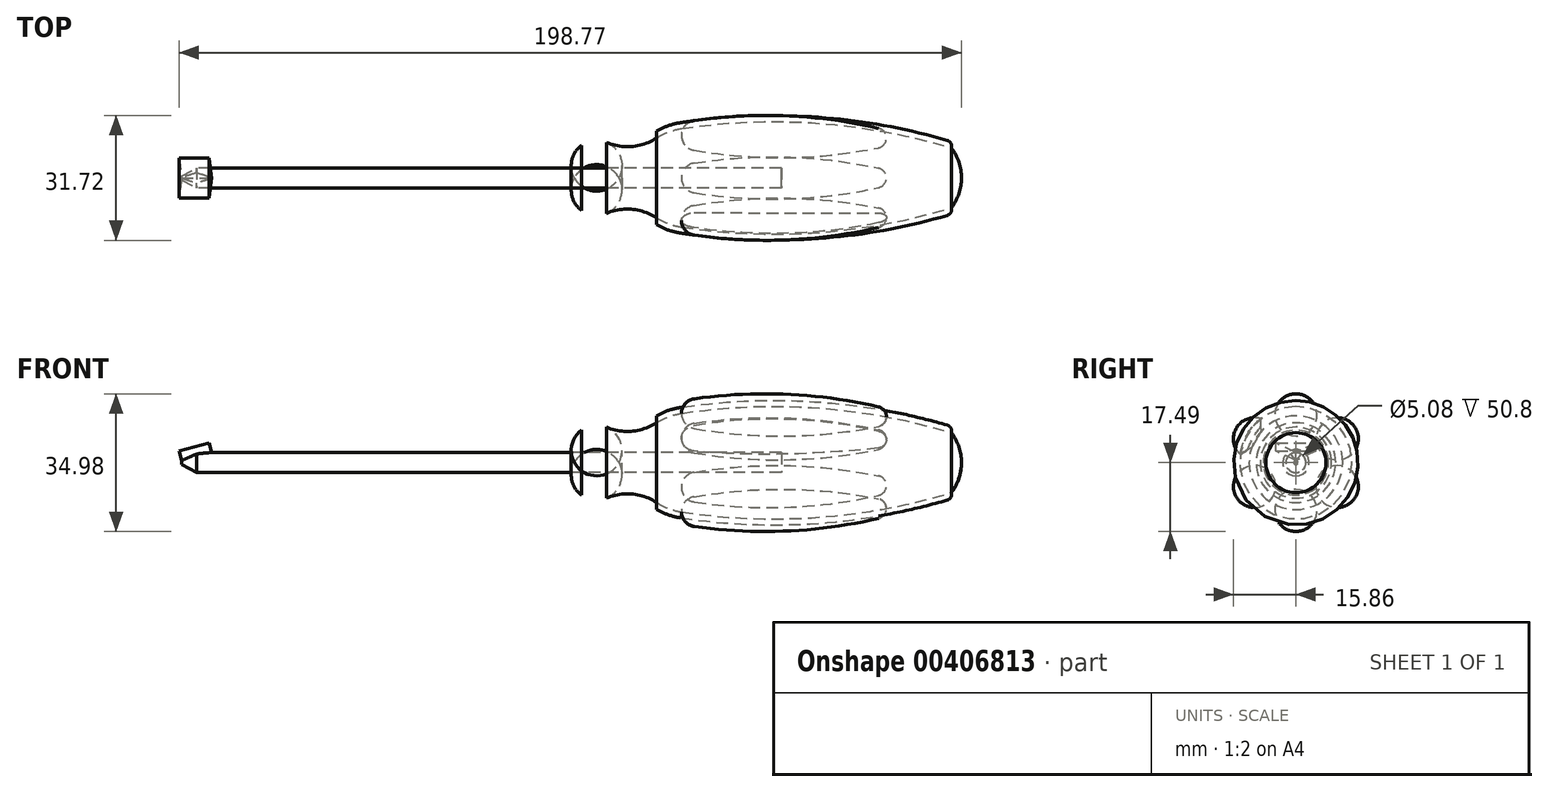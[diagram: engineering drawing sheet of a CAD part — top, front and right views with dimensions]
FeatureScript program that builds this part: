
annotation { "Feature Type Name" : "Feature", "Feature Type Description" : "" }
export const myFeature = defineFeature(function(context is Context, id is Id, definition is map)
    precondition{}
    {
        {
            var Q0;
            Q0=qCreatedBy(makeId("Front.planeOp"),FACE);
            var sketch = newSketch(context, id + "F0", { "sketchPlane" : qUnion([Q0])});
            skLineSegment(sketch, "E0", {"start": v(-101.6, 0) * mm, "end": v(96.52, 0) * mm});
            skLineSegment(sketch, "E1", {"start": v(96.52, 0) * mm, "end": v(117.55, 0) * mm, "construction": true});
            skLineSegment(sketch, "E2", {"start": v(50.8, 2.54) * mm, "end": v(-97.8, 2.54) * mm});
            skLineSegment(sketch, "E3", {"start": v(-101.6, 0.5) * mm, "end": v(-101.6, 0) * mm});
            skLineSegment(sketch, "E4", {"start": v(0, 2.54) * mm, "end": v(0, 8.25) * mm});
            skArc(sketch, "E5", {"start": v(6.35, 9.02) * mm, "mid": v(3.07, 9.48) * mm, "end": v(0, 8.25) * mm});
            skArc(sketch, "E6", {"start": v(6.35, 9.02) * mm, "mid": v(12.84, 7.99) * mm, "end": v(19.05, 10.11) * mm});
            skArc(sketch, "E7", {"start": v(25.4, 12.52) * mm, "mid": v(22.1, 11.65) * mm, "end": v(19.05, 10.11) * mm});
            skArc(sketch, "E8", {"start": v(93.98, 7.62) * mm, "mid": v(59.96, 13.9) * mm, "end": v(25.4, 12.52) * mm});
            skArc(sketch, "E9", {"start": v(96.52, 0) * mm, "mid": v(95.87, 4.02) * mm, "end": v(93.98, 7.62) * mm});
            skArc(sketch, "E10.0", {"start": v(25.17, 14.02) * mm, "mid": v(22.01, 13.24) * mm, "end": v(19.05, 11.9) * mm});
            skArc(sketch, "E10.1", {"start": v(92.95, 9.52) * mm, "mid": v(59.3, 15.46) * mm, "end": v(25.17, 14.02) * mm});
            skLineSegment(sketch, "E11", {"start": v(19.05, 11.9) * mm, "end": v(19.05, 10.11) * mm});
            skArc(sketch, "E12", {"start": v(93.98, 7.62) * mm, "mid": v(93.86, 8.78) * mm, "end": v(92.95, 9.52) * mm});
            skPoint(sketch, "E13.orphan", {"position": v(0, 0) * mm});
            skLineSegment(sketch, "E14", {"start": v(50.8, 2.54) * mm, "end": v(50.8, 0) * mm});
            skLineSegment(sketch, "E15", {"start": v(-101.6, 0.5) * mm, "end": v(-97.8, 2.54) * mm});
            skPoint(sketch, "E16.orphan", {"position": v(-101.6, 2.54) * mm});
            skSolve(sketch);
        }
        {
            var Q0;
            Q0=qCreatedBy(makeId("Front.planeOp"),FACE);
            var sketch = newSketch(context, id + "F1", { "sketchPlane" : qUnion([Q0])});
            skLineSegment(sketch, "E17", {"start": v(25.4, 12.52) * mm, "end": v(77.47, 11.64) * mm});
            skArc(sketch, "E18", {"start": v(28.67, 16.22) * mm, "mid": v(26.35, 14.97) * mm, "end": v(25.4, 12.52) * mm});
            skArc(sketch, "E19", {"start": v(77.47, 11.64) * mm, "mid": v(76.93, 13.25) * mm, "end": v(75.5, 14.16) * mm});
            skArc(sketch, "E20", {"start": v(75.5, 14.16) * mm, "mid": v(52.19, 17.37) * mm, "end": v(28.67, 16.22) * mm});
            skSolve(sketch);
        }
        {
            var Q0;
            Q0=qCreatedBy(makeId("Front.planeOp"),FACE);
            var sketch = newSketch(context, id + "F2", { "sketchPlane" : qUnion([Q0])});
            skLineSegment(sketch, "E21", {"start": v(-101.6, 0.5) * mm, "end": v(-93.98, 2.54) * mm});
            skSolve(sketch);
        }
        {
            var Q0;
            Q0=sQuery(id+"F2.wireOp",VERTEX,"E21.start");
            var Q1;
            Q1=sQuery(id+"F2.wireOp",EDGE,"E21");
            cPlane(context, id + "F3", {"entities" : qUnion([Q0, Q1]), "cplaneType" : CPlaneType.LINE_POINT, "offset" : 25.4 * mm, "width" : 152.4 * mm, "height" : 152.4 * mm});
        }
        {
            var Q0;
            Q0=qCreatedBy(id+"F3.planeOp",FACE);
            var sketch = newSketch(context, id + "F4", { "sketchPlane" : qUnion([Q0])});
            skLineSegment(sketch, "E22", {"start": v(5.08, 29.2) * mm, "end": v(0, 26.67) * mm});
            skLineSegment(sketch, "E23", {"start": v(0, 26.67) * mm, "end": v(-5.08, 29.2) * mm});
            skLineSegment(sketch, "E24", {"start": v(-5.08, 29.2) * mm, "end": v(5.08, 29.2) * mm});
            skLineSegment(sketch, "E25", {"start": v(0, 29.2) * mm, "end": v(0, 26.67) * mm, "construction": true});
            skSolve(sketch);
        }
        {
            var Q0;
            {var subQ0=sQuery(id+"F0.wireOp",EDGE,"E3");Q0=makeQuery(id+"F0.imprint","IMPRINT",FACE,{"disambiguationData":[TD([[makeQuery(id+"F0.imprint","IMPRINT",EDGE,{"derivedFrom":subQ0}),1.0]])]});}
            var Q1;
            Q1=sQuery(id+"F0.wireOp",EDGE,"E0");
            revolve(context, id + "F5", {"entities" : qUnion([Q0]), "axis" : qUnion([Q1]), "revolveType" : RevolveType.FULL});
        }
        {
            var Q0;
            {var subQ0=sQuery(id+"F0.wireOp",EDGE,"E4");Q0=makeQuery(id+"F0.imprint","IMPRINT",FACE,{"disambiguationData":[TD([[makeQuery(id+"F0.imprint","IMPRINT",EDGE,{"derivedFrom":subQ0}),-1.0]])]});}
            var Q1;
            Q1=sQuery(id+"F0.wireOp",EDGE,"E0");
            revolve(context, id + "F6", {"entities" : qUnion([Q0]), "axis" : qUnion([Q1]), "revolveType" : RevolveType.FULL});
        }
        {
            var Q0;
            Q0=makeQuery(id+"F0.imprint","IMPRINT",FACE,{"disambiguationData":[TD([[makeQuery(id+"F0.imprint","IMPRINT",EDGE,{"derivedFrom":sQuery(id+"F0.wireOp",EDGE,"E7")}),-1.0]])]});
            var Q1;
            Q1=sQuery(id+"F0.wireOp",EDGE,"E0");
            revolve(context, id + "F7", {"entities" : qUnion([Q0]), "axis" : qUnion([Q1]), "revolveType" : RevolveType.FULL});
        }
        {
            var Q0;
            Q0=makeQuery(id+"F1.imprint","IMPRINT",FACE,{"disambiguationData":[TD([[makeQuery(id+"F1.imprint","IMPRINT",EDGE,{"derivedFrom":sQuery(id+"F1.wireOp",EDGE,"E17")}),1.0]])]});
            var Q1;
            Q1=sQuery(id+"F1.wireOp",EDGE,"E17");
            revolve(context, id + "F8", {"entities" : qUnion([Q0]), "axis" : qUnion([Q1]), "revolveType" : RevolveType.FULL});
        }
        {
            var Q0;
            Q0=makeQuery(id+"F8.opRevolve","SWEPT_BODY",BODY,{"disambiguationData":[OSD([sQuery(id+"F1.wireOp",EDGE,"E17"),sQuery(id+"F1.wireOp",EDGE,"E18"),sQuery(id+"F1.wireOp",EDGE,"E19"),sQuery(id+"F1.wireOp",EDGE,"E20")])]});
            var Q1;
            Q1=makeQuery(id+"F7.opRevolve","SWEPT_FACE",FACE,{"disambiguationData":[OSD([sQuery(id+"F0.wireOp",EDGE,"E10.1")])]});
            circularPattern(context, id + "F9", {"entities" : qUnion([Q0]), "axis" : qUnion([Q1]), "angle" : 360 * degree, "instanceCount" : 6, "equalSpace" : true});
        }
        {
            var Q0;
            Q0=makeQuery(id+"F6.opRevolve","SWEPT_BODY",BODY,{"disambiguationData":[OSD([sQuery(id+"F0.wireOp",EDGE,"E0"),sQuery(id+"F0.wireOp",EDGE,"E2"),sQuery(id+"F0.wireOp",EDGE,"E4"),sQuery(id+"F0.wireOp",EDGE,"E5"),sQuery(id+"F0.wireOp",EDGE,"E6"),sQuery(id+"F0.wireOp",EDGE,"E7"),sQuery(id+"F0.wireOp",EDGE,"E8"),sQuery(id+"F0.wireOp",EDGE,"E9"),sQuery(id+"F0.wireOp",EDGE,"E14")])]});
            var Q1;
            Q1=makeQuery(id+"F9.opPattern","COPY",BODY,{"derivedFrom":makeQuery(id+"F8.opRevolve","SWEPT_BODY",BODY,{"disambiguationData":[OSD([sQuery(id+"F1.wireOp",EDGE,"E17"),sQuery(id+"F1.wireOp",EDGE,"E18"),sQuery(id+"F1.wireOp",EDGE,"E19"),sQuery(id+"F1.wireOp",EDGE,"E20")])]}),"instanceName":"5"});
            booleanBodies(context, id + "F10", {"operationType" : BooleanOperationType.SUBTRACTION, "tools" : qUnion([Q0]), "targets" : qUnion([Q1]), "keepTools" : true});
        }
        {
            var Q0;
            Q0=makeQuery(id+"F4.imprint","IMPRINT",FACE,{"disambiguationData":[TD([[makeQuery(id+"F4.imprint","IMPRINT",EDGE,{"derivedFrom":sQuery(id+"F4.wireOp",EDGE,"E22")}),-1.0]])]});
            var Q1;
            Q1=sQuery(id+"F2.wireOp",EDGE,"E21");
            sweep(context, id + "F11", {"operationType" : NewBodyOperationType.REMOVE, "profiles" : qUnion([Q0]), "path" : qUnion([Q1])});
        }
        {
            var Q0;
            Q0=makeQuery(id+"F4.imprint","IMPRINT",FACE,{"disambiguationData":[TD([[makeQuery(id+"F4.imprint","IMPRINT",EDGE,{"derivedFrom":sQuery(id+"F4.wireOp",EDGE,"E22")}),-1.0]])]});
            var Q1;
            Q1=qConstructionFilter(qBodyType(qCreatedBy(id+"F2",EDGE),BodyType.WIRE),ConstructionObject.NO);
            sweep(context, id + "F12", {"profiles" : qUnion([Q0]), "path" : qUnion([Q1])});
        }
    });
